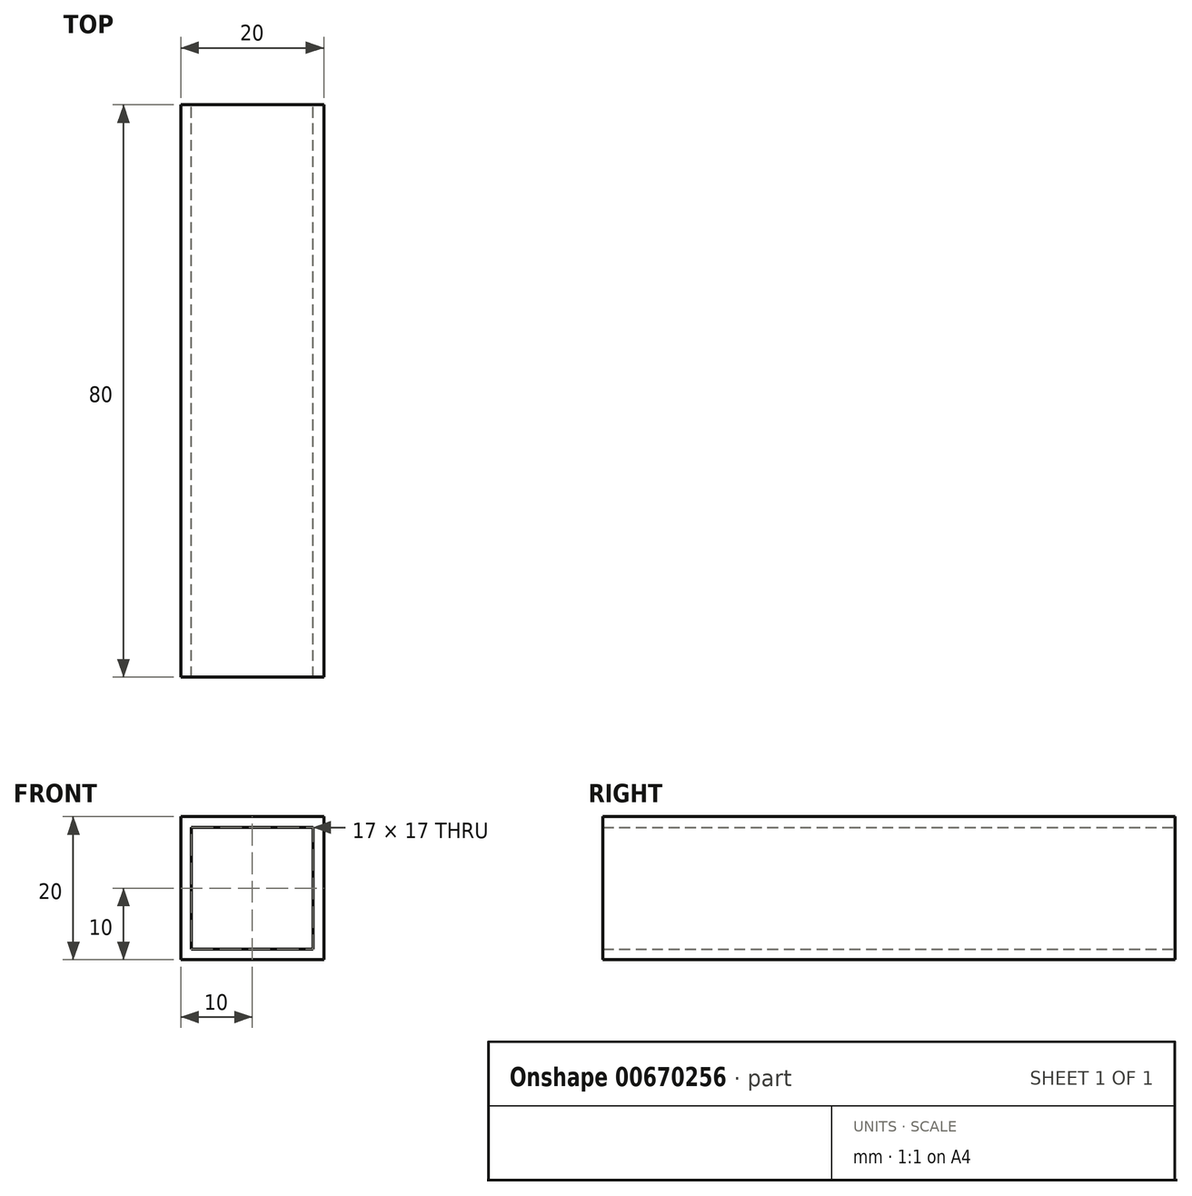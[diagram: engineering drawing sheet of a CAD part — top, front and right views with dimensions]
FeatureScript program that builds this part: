
annotation { "Feature Type Name" : "Feature", "Feature Type Description" : "" }
export const myFeature = defineFeature(function(context is Context, id is Id, definition is map)
    precondition{}
    {
        {
            var Q0;
            Q0=qCreatedBy(makeId("Front.planeOp"),FACE);
            var sketch = newSketch(context, id + "F0", { "sketchPlane" : qUnion([Q0])});
            skLineSegment(sketch, "E0.bottom", {"start": v(-10, 10) * mm, "end": v(10, 10) * mm});
            skLineSegment(sketch, "E0.top", {"start": v(-10, -10) * mm, "end": v(10, -10) * mm});
            skLineSegment(sketch, "E0.left", {"start": v(-10, 10) * mm, "end": v(-10, -10) * mm});
            skLineSegment(sketch, "E0.right", {"start": v(10, 10) * mm, "end": v(10, -10) * mm});
            skLineSegment(sketch, "E1.bottom", {"start": v(-8.5, 8.5) * mm, "end": v(8.5, 8.5) * mm});
            skLineSegment(sketch, "E1.top", {"start": v(-8.5, -8.5) * mm, "end": v(8.5, -8.5) * mm});
            skLineSegment(sketch, "E1.left", {"start": v(-8.5, 8.5) * mm, "end": v(-8.5, -8.5) * mm});
            skLineSegment(sketch, "E1.right", {"start": v(8.5, 8.5) * mm, "end": v(8.5, -8.5) * mm});
            skSolve(sketch);
        }
        {
            var Q0;
            Q0 = qSketchRegion(id + "F0", true);
            extrude(context, id + "F1", {"entities" : qUnion([Q0]), "depth" : 80 * mm, "offsetDistance" : 25 * mm});
        }
    });
